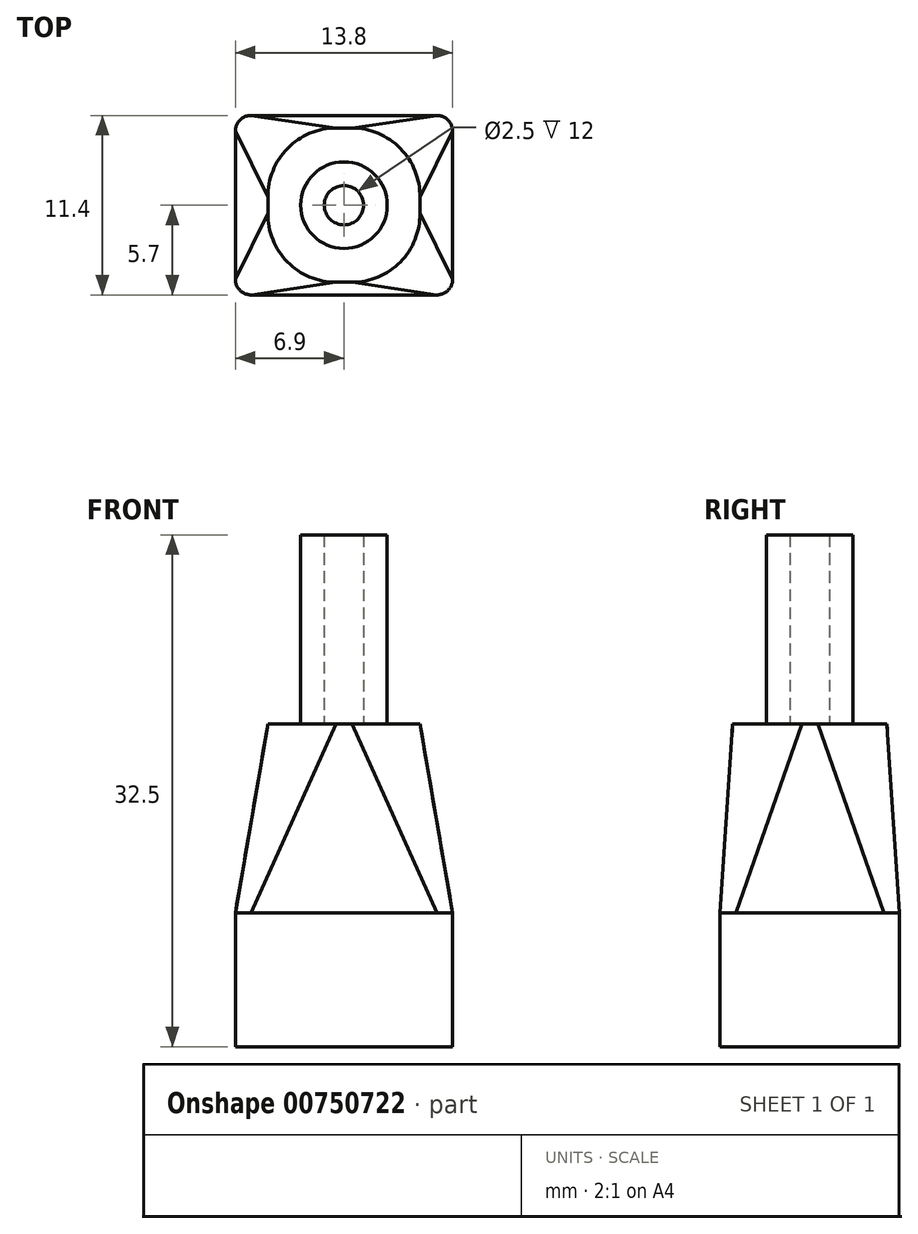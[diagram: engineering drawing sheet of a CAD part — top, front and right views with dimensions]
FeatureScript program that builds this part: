
annotation { "Feature Type Name" : "Feature", "Feature Type Description" : "" }
export const myFeature = defineFeature(function(context is Context, id is Id, definition is map)
    precondition{}
    {
        {
            var Q0;
            Q0=qCreatedBy(makeId("Top.planeOp"),FACE);
            var sketch = newSketch(context, id + "F0", { "sketchPlane" : qUnion([Q0])});
            skLineSegment(sketch, "E0.bottom", {"start": v(5.9, -5.7) * mm, "end": v(-5.9, -5.7) * mm});
            skLineSegment(sketch, "E0.top", {"start": v(5.9, 5.7) * mm, "end": v(-5.9, 5.7) * mm});
            skLineSegment(sketch, "E0.left", {"start": v(6.9, -4.7) * mm, "end": v(6.9, 4.7) * mm});
            skLineSegment(sketch, "E0.right", {"start": v(-6.9, -4.7) * mm, "end": v(-6.9, 4.7) * mm});
            skPoint(sketch, "E0.middle", {"position": v(0, 0) * mm});
            skPoint(sketch, "E1.visualSharp", {"position": v(-6.9, 5.7) * mm});
            skArc(sketch, "E1.filletArc", {"start": v(-5.9, 5.7) * mm, "mid": v(-6.6, 5.4) * mm, "end": v(-6.9, 4.7) * mm});
            skPoint(sketch, "E2.visualSharp", {"position": v(6.9, 5.7) * mm});
            skArc(sketch, "E2.filletArc", {"start": v(6.9, 4.7) * mm, "mid": v(6.6, 5.4) * mm, "end": v(5.9, 5.7) * mm});
            skPoint(sketch, "E3.visualSharp", {"position": v(6.9, -5.7) * mm});
            skArc(sketch, "E3.filletArc", {"start": v(5.9, -5.7) * mm, "mid": v(6.6, -5.4) * mm, "end": v(6.9, -4.7) * mm});
            skPoint(sketch, "E4.visualSharp", {"position": v(-6.9, -5.7) * mm});
            skArc(sketch, "E4.filletArc", {"start": v(-6.9, -4.7) * mm, "mid": v(-6.6, -5.4) * mm, "end": v(-5.9, -5.7) * mm});
            skSolve(sketch);
        }
        {
            var Q0;
            Q0 = qSketchRegion(id + "F0", true);
            extrude(context, id + "F1", {"entities" : qUnion([Q0]), "depth" : 8.5 * mm, "offsetDistance" : 25 * mm});
        }
        {
            var Q0;
            Q0=makeQuery(id+"F1.opExtrude","CAP_FACE",FACE,{"disambiguationData":[OSD([sQuery(id+"F0.wireOp",EDGE,"E0.bottom"),sQuery(id+"F0.wireOp",EDGE,"E0.top"),sQuery(id+"F0.wireOp",EDGE,"E0.left"),sQuery(id+"F0.wireOp",EDGE,"E0.right")])],"isStart":false});
            cPlane(context, id + "F2", {"entities" : qUnion([Q0]), "cplaneType" : CPlaneType.OFFSET, "offset" : 12 * mm, "width" : 150 * mm, "height" : 150 * mm});
        }
        {
            var Q0;
            Q0=qCreatedBy(id+"F2.planeOp",FACE);
            var sketch = newSketch(context, id + "F3", { "sketchPlane" : qUnion([Q0])});
            skLineSegment(sketch, "E5", {"start": v(-0.5, 4.9) * mm, "end": v(0.5, 4.9) * mm});
            skLineSegment(sketch, "E6", {"start": v(-0.5, -4.9) * mm, "end": v(0.5, -4.9) * mm});
            skLineSegment(sketch, "E7", {"start": v(4.83, 0.5) * mm, "end": v(4.83, -0.5) * mm});
            skLineSegment(sketch, "E8", {"start": v(-4.83, 0.5) * mm, "end": v(-4.83, -0.5) * mm});
            skPoint(sketch, "E9", {"position": v(-4.83, 0) * mm});
            skPoint(sketch, "E10", {"position": v(4.83, 0) * mm});
            skPoint(sketch, "E11", {"position": v(0, 4.9) * mm});
            skPoint(sketch, "E12", {"position": v(0, -4.9) * mm});
            skArc(sketch, "E13", {"start": v(-0.5, 4.9) * mm, "mid": v(-3.58, 3.6) * mm, "end": v(-4.82, 0.5) * mm});
            skArc(sketch, "E14", {"start": v(4.83, 0.5) * mm, "mid": v(3.58, 3.6) * mm, "end": v(0.5, 4.9) * mm});
            skArc(sketch, "E15", {"start": v(0.5, -4.9) * mm, "mid": v(3.58, -3.6) * mm, "end": v(4.83, -0.5) * mm});
            skArc(sketch, "E16", {"start": v(-4.82, -0.5) * mm, "mid": v(-3.58, -3.6) * mm, "end": v(-0.5, -4.9) * mm});
            skLineSegment(sketch, "E17", {"start": v(-4.83, 0) * mm, "end": v(4.83, 0) * mm, "construction": true});
            skPoint(sketch, "E18", {"position": v(0, 0) * mm});
            skLineSegment(sketch, "E19", {"start": v(0, 4.9) * mm, "end": v(0, -4.9) * mm, "construction": true});
            skSolve(sketch);
        }
        {
            var Q1;
            Q1=makeQuery(id+"F1.opExtrude","CAP_FACE",FACE,{"disambiguationData":[OSD([sQuery(id+"F0.wireOp",EDGE,"E0.bottom"),sQuery(id+"F0.wireOp",EDGE,"E0.top"),sQuery(id+"F0.wireOp",EDGE,"E0.left"),sQuery(id+"F0.wireOp",EDGE,"E0.right"),sQuery(id+"F0.wireOp",EDGE,"E1.filletArc"),sQuery(id+"F0.wireOp",EDGE,"E2.filletArc"),sQuery(id+"F0.wireOp",EDGE,"E3.filletArc"),sQuery(id+"F0.wireOp",EDGE,"E4.filletArc")])],"isStart":false});
            var Q2;
            Q2=makeQuery(id+"F3.imprint","IMPRINT",FACE,{"disambiguationData":[TD([[makeQuery(id+"F3.imprint","IMPRINT",EDGE,{"derivedFrom":sQuery(id+"F3.wireOp",EDGE,"E5")}),-1.0]])]});
            loft(context, id + "F4", {"operationType" : NewBodyOperationType.ADD, "sheetProfilesArray" : [{ "sheetProfileEntities" : qUnion([Q1]) }, { "sheetProfileEntities" : qUnion([Q2]) }]});
        }
        {
            var Q0;
            Q0=makeQuery(id+"F4.opLoft","CAP_FACE",FACE,{"disambiguationData":[OSD([makeQuery(id+"F3.imprint","IMPRINT",FACE,{"disambiguationData":[TD([[makeQuery(id+"F3.imprint","IMPRINT",EDGE,{"derivedFrom":sQuery(id+"F3.wireOp",EDGE,"E5")}),-1.0]])]})])],"isStart":true});
            var sketch = newSketch(context, id + "F5", { "sketchPlane" : qUnion([Q0])});
            skCircle(sketch, "E20", {"center": v(0, 0) * mm, "radius": 2.75 * mm});
            skCircle(sketch, "E21", {"center": v(0, 0) * mm, "radius": 1.25 * mm});
            skSolve(sketch);
        }
        {
            var Q0;
            Q0 = qSketchRegion(id + "F5", true);
            extrude(context, id + "F6", {"entities" : qUnion([Q0]), "operationType" : NewBodyOperationType.ADD, "depth" : 12 * mm, "offsetDistance" : 25 * mm});
        }
    });
